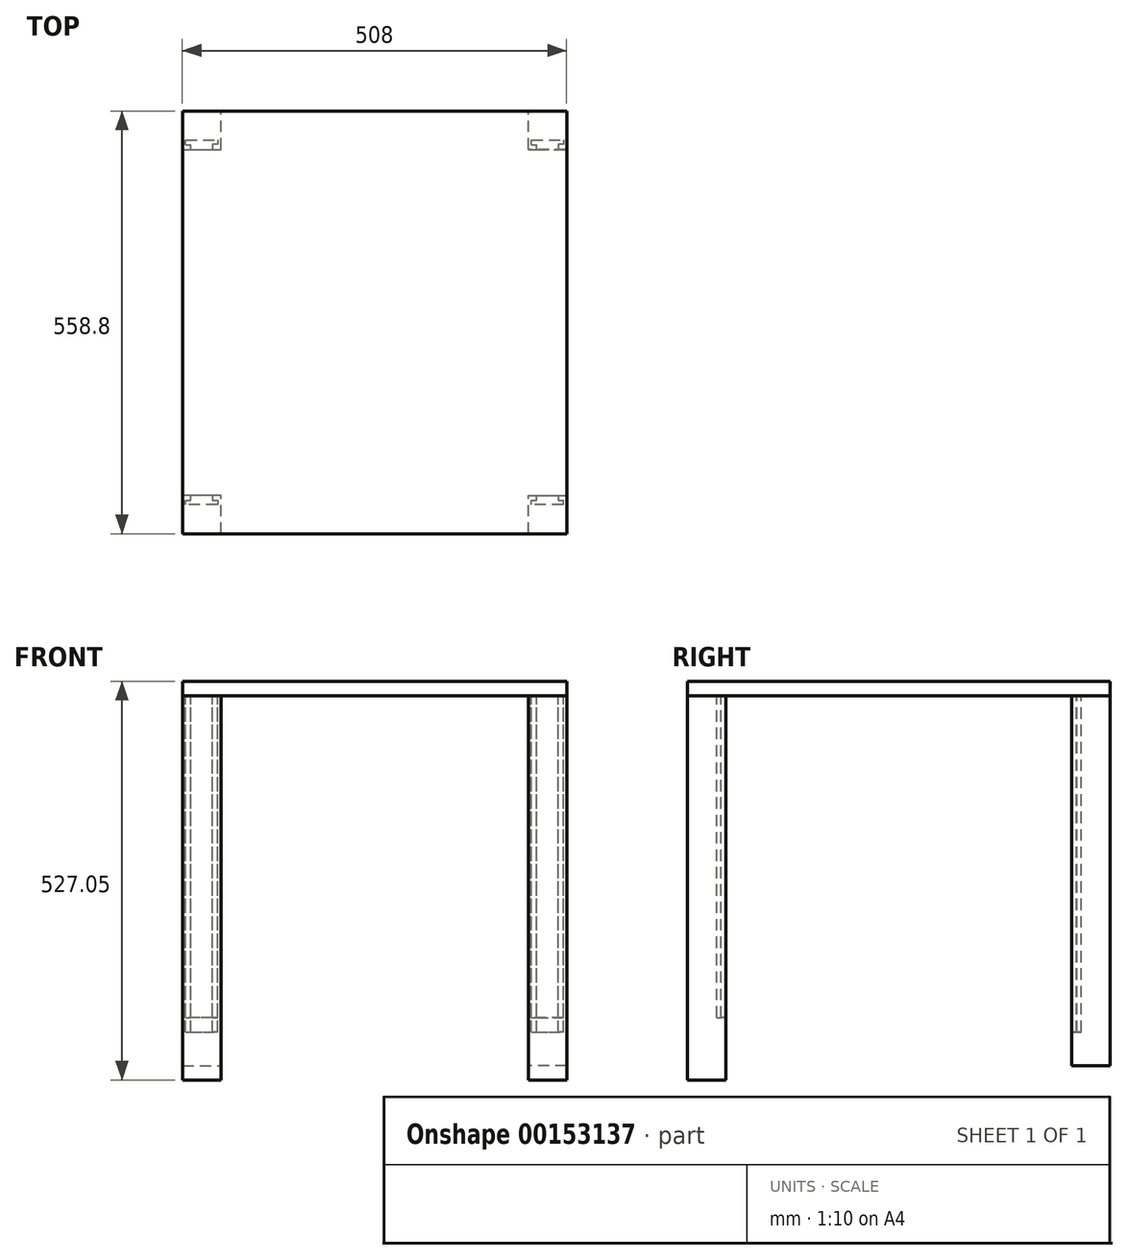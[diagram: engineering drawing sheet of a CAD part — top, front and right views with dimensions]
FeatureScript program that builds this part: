
annotation { "Feature Type Name" : "Feature", "Feature Type Description" : "" }
export const myFeature = defineFeature(function(context is Context, id is Id, definition is map)
    precondition{}
    {
        {
            var Q0;
            Q0=qCreatedBy(makeId("Front.planeOp"),FACE);
            var sketch = newSketch(context, id + "F0", { "sketchPlane" : qUnion([Q0])});
            skLineSegment(sketch, "E0.bottom", {"start": v(-241.12, 387.24) * mm, "end": v(266.88, 387.24) * mm});
            skLineSegment(sketch, "E0.top", {"start": v(-241.12, 368.2) * mm, "end": v(266.88, 368.2) * mm});
            skLineSegment(sketch, "E0.left", {"start": v(-241.12, 387.24) * mm, "end": v(-241.12, 368.2) * mm});
            skLineSegment(sketch, "E0.right", {"start": v(266.88, 387.24) * mm, "end": v(266.88, 368.2) * mm});
            skLineSegment(sketch, "E1", {"start": v(-241.12, 368.2) * mm, "end": v(-241.12, -120.76) * mm});
            skLineSegment(sketch, "E2", {"start": v(266.88, 368.2) * mm, "end": v(266.88, -120.76) * mm});
            skLineSegment(sketch, "E3", {"start": v(-241.12, -120.76) * mm, "end": v(-190.32, -120.76) * mm});
            skLineSegment(sketch, "E4", {"start": v(-190.32, -120.76) * mm, "end": v(-190.32, 368.2) * mm});
            skLineSegment(sketch, "E5", {"start": v(266.88, -120.76) * mm, "end": v(216.08, -120.76) * mm});
            skLineSegment(sketch, "E6", {"start": v(216.08, -120.76) * mm, "end": v(216.08, 368.2) * mm});
            skSolve(sketch);
        }
        {
            var Q0;
            {var subQ0=sQuery(id+"F0.wireOp",EDGE,"E1");Q0=makeQuery(id+"F0.imprint","IMPRINT",FACE,{"disambiguationData":[TD([[makeQuery(id+"F0.imprint","IMPRINT",EDGE,{"derivedFrom":subQ0}),1.0]])]});}
            var Q1;
            {var subQ0=sQuery(id+"F0.wireOp",EDGE,"E2");Q1=makeQuery(id+"F0.imprint","IMPRINT",FACE,{"disambiguationData":[TD([[makeQuery(id+"F0.imprint","IMPRINT",EDGE,{"derivedFrom":subQ0}),-1.0]])]});}
            extrude(context, id + "F1", {"entities" : qUnion([Q0, Q1]), "depth" : 50.8 * mm});
        }
        {
            var Q0;
            {var subQ0=sQuery(id+"F0.wireOp",EDGE,"E0.top");Q0=makeQuery(id+"F1.opExtrude","SWEPT_FACE",FACE,{"disambiguationData":[OSD([subQ0]),TDD([makeQuery(id+"F0.imprint","IMPRINT",EDGE,{"disambiguationData":[TD([[makeQuery(id+"F0.imprint","INTERSECT",VERTEX,{"derivedFrom":[subQ0,sQuery(id+"F0.wireOp",EDGE,"E6")]}),-1.0]])],"derivedFrom":subQ0})])]});}
            var sketch = newSketch(context, id + "F2", { "sketchPlane" : qUnion([Q0])});
            skLineSegment(sketch, "E7", {"start": v(-229.94, -50.8) * mm, "end": v(-229.94, -44.79) * mm});
            skLineSegment(sketch, "E8", {"start": v(-236.8, -44.79) * mm, "end": v(-236.8, -38.35) * mm});
            skPoint(sketch, "E8.startSnap0", {"position": v(-229.94, -44.79) * mm});
            skLineSegment(sketch, "E9", {"start": v(-236.8, -38.35) * mm, "end": v(-194.63, -38.35) * mm});
            skLineSegment(sketch, "E10", {"start": v(-194.63, -38.35) * mm, "end": v(-194.63, -44.12) * mm});
            skLineSegment(sketch, "E11", {"start": v(-194.63, -44.12) * mm, "end": v(-201.5, -44.12) * mm});
            skLineSegment(sketch, "E12", {"start": v(-201.5, -44.12) * mm, "end": v(-201.5, -50.8) * mm});
            skLineSegment(sketch, "E13", {"start": v(-236.8, -44.79) * mm, "end": v(-229.94, -44.79) * mm});
            skLineSegment(sketch, "E14", {"start": v(-229.94, -50.8) * mm, "end": v(-201.5, -50.8) * mm});
            skSolve(sketch);
        }
        {
            var Q0;
            Q0=makeQuery(id+"F2.imprint","IMPRINT",FACE,{"disambiguationData":[TD([[makeQuery(id+"F2.imprint","IMPRINT",EDGE,{"derivedFrom":sQuery(id+"F2.wireOp",EDGE,"E7")}),-1.0]])]});
            extrude(context, id + "F3", {"entities" : qUnion([Q0]), "operationType" : NewBodyOperationType.REMOVE, "oppositeDirection" : true, "depth" : 444.5 * mm});
        }
        {
            var Q0;
            {var subQ0=sQuery(id+"F0.wireOp",EDGE,"E0.top");Q0=makeQuery(id+"F1.opExtrude","SWEPT_FACE",FACE,{"disambiguationData":[OSD([subQ0]),TDD([makeQuery(id+"F0.imprint","IMPRINT",EDGE,{"disambiguationData":[TD([[makeQuery(id+"F0.imprint","INTERSECT",VERTEX,{"derivedFrom":[subQ0,sQuery(id+"F0.wireOp",EDGE,"E6")]}),-1.0]])],"derivedFrom":subQ0})])]});}
            var sketch = newSketch(context, id + "F4", { "sketchPlane" : qUnion([Q0])});
            skLineSegment(sketch, "E15", {"start": v(227.26, -50.8) * mm, "end": v(227.26, -44.79) * mm});
            skLineSegment(sketch, "E16", {"start": v(220.4, -44.79) * mm, "end": v(220.4, -38.35) * mm});
            skPoint(sketch, "E16.startSnap0", {"position": v(227.26, -44.79) * mm});
            skLineSegment(sketch, "E17", {"start": v(220.4, -38.35) * mm, "end": v(262.57, -38.35) * mm});
            skLineSegment(sketch, "E18", {"start": v(262.57, -38.35) * mm, "end": v(262.57, -44.12) * mm});
            skLineSegment(sketch, "E19", {"start": v(262.57, -44.12) * mm, "end": v(255.7, -44.12) * mm});
            skLineSegment(sketch, "E20", {"start": v(255.7, -44.12) * mm, "end": v(255.7, -50.8) * mm});
            skLineSegment(sketch, "E21", {"start": v(220.4, -44.79) * mm, "end": v(227.26, -44.79) * mm});
            skLineSegment(sketch, "E22", {"start": v(227.26, -50.8) * mm, "end": v(255.7, -50.8) * mm});
            skSolve(sketch);
        }
        {
            var Q0;
            Q0=makeQuery(id+"F4.imprint","IMPRINT",FACE,{"disambiguationData":[TD([[makeQuery(id+"F4.imprint","IMPRINT",EDGE,{"derivedFrom":sQuery(id+"F4.wireOp",EDGE,"E15")}),-1.0]])]});
            extrude(context, id + "F5", {"entities" : qUnion([Q0]), "operationType" : NewBodyOperationType.REMOVE, "oppositeDirection" : true, "depth" : 444.5 * mm});
        }
        {
            var Q0;
            Q0=makeQuery(id+"F0.imprint","IMPRINT",FACE,{"disambiguationData":[TD([[makeQuery(id+"F0.imprint","IMPRINT",EDGE,{"derivedFrom":sQuery(id+"F0.wireOp",EDGE,"E0.bottom")}),-1.0]])]});
            extrude(context, id + "F6", {"entities" : qUnion([Q0]), "depth" : 558.8 * mm});
        }
        {
            var Q0;
            Q0=makeQuery(id+"F6.opExtrude","SWEPT_FACE",FACE,{"disambiguationData":[OSD([sQuery(id+"F0.wireOp",EDGE,"E0.bottom")])]});
            var sketch = newSketch(context, id + "F7", { "sketchPlane" : qUnion([Q0])});
            skPoint(sketch, "E23", {"position": v(-241.12, -558.8) * mm});
            skPoint(sketch, "E24", {"position": v(266.88, -558.8) * mm});
            skPoint(sketch, "E25", {"position": v(-241.12, -508) * mm});
            skPoint(sketch, "E26", {"position": v(216.08, -558.8) * mm});
            skLineSegment(sketch, "E27", {"start": v(-241.12, -508) * mm, "end": v(-241.12, -558.8) * mm});
            skLineSegment(sketch, "E28", {"start": v(-190.32, -558.8) * mm, "end": v(-241.12, -558.8) * mm});
            skLineSegment(sketch, "E29", {"start": v(-190.32, -558.8) * mm, "end": v(-190.32, -508) * mm});
            skLineSegment(sketch, "E30", {"start": v(-190.32, -508) * mm, "end": v(-241.12, -508) * mm});
            skLineSegment(sketch, "E31", {"start": v(216.08, -558.8) * mm, "end": v(216.08, -508) * mm});
            skLineSegment(sketch, "E32", {"start": v(216.08, -508) * mm, "end": v(266.88, -508) * mm});
            skLineSegment(sketch, "E33", {"start": v(266.88, -558.8) * mm, "end": v(266.88, -508) * mm});
            skLineSegment(sketch, "E34", {"start": v(216.08, -558.8) * mm, "end": v(266.88, -558.8) * mm});
            skPoint(sketch, "E35", {"position": v(255.7, -508) * mm});
            skPoint(sketch, "E36", {"position": v(262.57, -514.68) * mm});
            skPoint(sketch, "E37", {"position": v(262.57, -520.45) * mm});
            skPoint(sketch, "E38", {"position": v(220.4, -520.45) * mm});
            skPoint(sketch, "E39", {"position": v(220.4, -514.68) * mm});
            skPoint(sketch, "E40", {"position": v(227.26, -508) * mm});
            skLineSegment(sketch, "E41", {"start": v(262.57, -520.45) * mm, "end": v(220.4, -520.45) * mm});
            skLineSegment(sketch, "E42", {"start": v(220.4, -520.45) * mm, "end": v(220.4, -514.68) * mm});
            skLineSegment(sketch, "E43", {"start": v(220.4, -514.68) * mm, "end": v(227.26, -514.68) * mm});
            skLineSegment(sketch, "E44", {"start": v(227.26, -514.68) * mm, "end": v(227.26, -508) * mm});
            skLineSegment(sketch, "E45", {"start": v(227.26, -508) * mm, "end": v(255.7, -508) * mm});
            skLineSegment(sketch, "E46", {"start": v(255.7, -508) * mm, "end": v(255.7, -514.68) * mm});
            skLineSegment(sketch, "E47", {"start": v(255.7, -514.68) * mm, "end": v(262.57, -514.68) * mm});
            skLineSegment(sketch, "E48", {"start": v(262.57, -520.45) * mm, "end": v(262.57, -514.68) * mm});
            skPoint(sketch, "E49", {"position": v(-201.5, -508) * mm});
            skPoint(sketch, "E50", {"position": v(-229.94, -508) * mm});
            skPoint(sketch, "E51", {"position": v(216.08, -508) * mm});
            skPoint(sketch, "E52", {"position": v(-201.5, -514.68) * mm});
            skPoint(sketch, "E53", {"position": v(-229.94, -514.68) * mm});
            skPoint(sketch, "E54", {"position": v(-194.63, -514.68) * mm});
            skPoint(sketch, "E55", {"position": v(-236.8, -514.68) * mm});
            skPoint(sketch, "E56", {"position": v(-194.63, -520.45) * mm});
            skPoint(sketch, "E57", {"position": v(-236.8, -520.45) * mm});
            skLineSegment(sketch, "E58", {"start": v(-194.63, -520.45) * mm, "end": v(-236.8, -520.45) * mm});
            skLineSegment(sketch, "E59", {"start": v(-236.8, -520.45) * mm, "end": v(-236.8, -514.68) * mm});
            skLineSegment(sketch, "E60", {"start": v(-236.8, -514.68) * mm, "end": v(-229.94, -514.68) * mm});
            skLineSegment(sketch, "E61", {"start": v(-229.94, -514.68) * mm, "end": v(-229.94, -508) * mm});
            skLineSegment(sketch, "E62", {"start": v(-229.94, -508) * mm, "end": v(-201.5, -508) * mm});
            skLineSegment(sketch, "E63", {"start": v(-201.5, -508) * mm, "end": v(-201.5, -514.68) * mm});
            skLineSegment(sketch, "E64", {"start": v(-201.5, -514.68) * mm, "end": v(-194.63, -514.68) * mm});
            skLineSegment(sketch, "E65", {"start": v(-194.63, -514.68) * mm, "end": v(-194.63, -520.45) * mm});
            skSolve(sketch);
        }
        {
            var Q0;
            {var subQ1=sQuery(id+"F7.wireOp",EDGE,"E31");Q0=makeQuery(id+"F7.imprint","IMPRINT",FACE,{"disambiguationData":[TD([[makeQuery(id+"F7.imprint","IMPRINT",EDGE,{"derivedFrom":subQ1}),-1.0]])]});}
            var Q1;
            {var subQ2=sQuery(id+"F7.wireOp",EDGE,"E27");Q1=makeQuery(id+"F7.imprint","IMPRINT",FACE,{"disambiguationData":[TD([[makeQuery(id+"F7.imprint","IMPRINT",EDGE,{"derivedFrom":subQ2}),-1.0]])]});}
            var Q2;
            Q2=makeQuery(id+"F7.imprint","IMPRINT",FACE,{"disambiguationData":[TD([[makeQuery(id+"F7.imprint","IMPRINT",EDGE,{"derivedFrom":sQuery(id+"F7.wireOp",EDGE,"E58")}),-1.0]])]});
            var Q3;
            Q3=makeQuery(id+"F7.imprint","IMPRINT",FACE,{"disambiguationData":[TD([[makeQuery(id+"F7.imprint","IMPRINT",EDGE,{"derivedFrom":sQuery(id+"F7.wireOp",EDGE,"E41")}),-1.0]])]});
            extrude(context, id + "F8", {"entities" : qUnion([Q0, Q1, Q2, Q3]), "oppositeDirection" : true, "depth" : 527.05 * mm, "hasSecondDirection" : true, "secondDirectionOppositeDirection" : true, "secondDirectionDepth" : 19.05 * mm});
        }
        {
            var Q0;
            Q0=makeQuery(id+"F7.imprint","IMPRINT",FACE,{"disambiguationData":[TD([[makeQuery(id+"F7.imprint","IMPRINT",EDGE,{"derivedFrom":sQuery(id+"F7.wireOp",EDGE,"E58")}),-1.0]])]});
            var Q1;
            Q1=makeQuery(id+"F7.imprint","IMPRINT",FACE,{"disambiguationData":[TD([[makeQuery(id+"F7.imprint","IMPRINT",EDGE,{"derivedFrom":sQuery(id+"F7.wireOp",EDGE,"E41")}),-1.0]])]});
            extrude(context, id + "F9", {"entities" : qUnion([Q0, Q1]), "operationType" : NewBodyOperationType.REMOVE, "oppositeDirection" : true, "depth" : 444.5 * mm, "hasSecondDirection" : true, "secondDirectionOppositeDirection" : true, "secondDirectionDepth" : 19.05 * mm});
        }
        {
            var Q0;
            Q0=makeQuery(id+"F7.imprint","IMPRINT",FACE,{"disambiguationData":[TD([[makeQuery(id+"F7.imprint","IMPRINT",EDGE,{"derivedFrom":sQuery(id+"F7.wireOp",EDGE,"E41")}),-1.0]])]});
            extrude(context, id + "F10", {"entities" : qUnion([Q0]), "operationType" : NewBodyOperationType.REMOVE, "oppositeDirection" : true, "depth" : 444.5 * mm, "hasSecondDirection" : true, "secondDirectionOppositeDirection" : true, "secondDirectionDepth" : 19.05 * mm});
        }
    });
